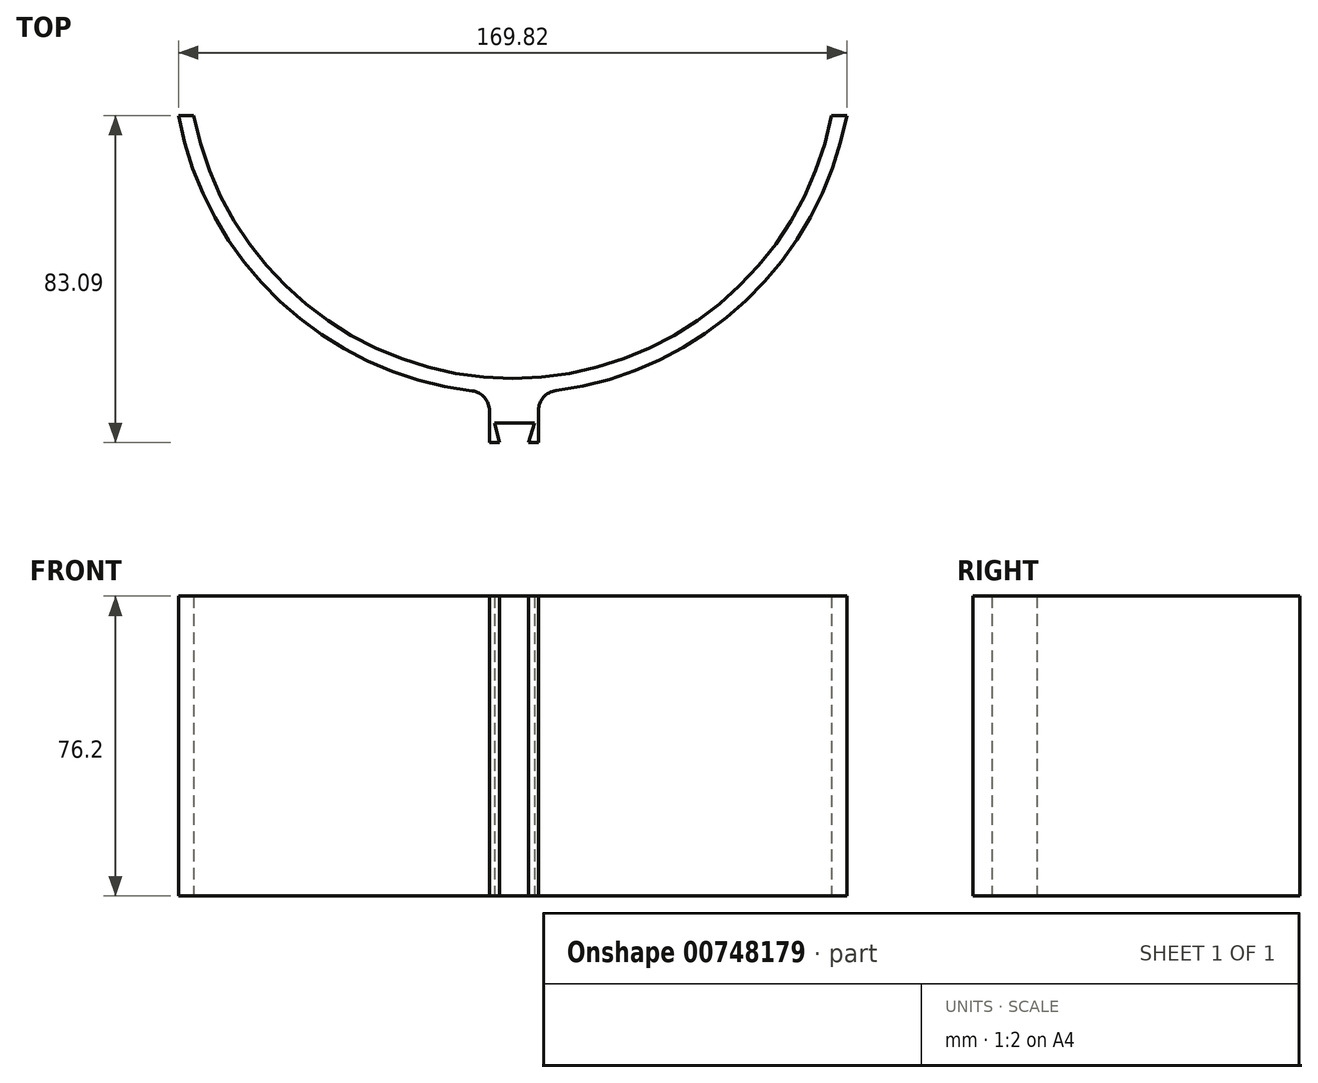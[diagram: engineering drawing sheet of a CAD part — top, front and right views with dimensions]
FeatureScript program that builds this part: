
annotation { "Feature Type Name" : "Feature", "Feature Type Description" : "" }
export const myFeature = defineFeature(function(context is Context, id is Id, definition is map)
    precondition{}
    {
        {
            var Q0;
            Q0=qCreatedBy(makeId("Top.planeOp"),FACE);
            var sketch = newSketch(context, id + "F0", { "sketchPlane" : qUnion([Q0])});
            skArc(sketch, "E0", {"start": v(-81.03, -15.77) * mm, "mid": v(0, -82.55) * mm, "end": v(81.03, -15.77) * mm});
            skArc(sketch, "E1", {"start": v(-84.9, -15.77) * mm, "mid": v(-57.43, -64.5) * mm, "end": v(-5.85, -86.16) * mm});
            skLineSegment(sketch, "E2", {"start": v(6.59, -98.8) * mm, "end": v(6.59, -86.1) * mm});
            skLineSegment(sketch, "E3", {"start": v(-5.85, -86.16) * mm, "end": v(-5.85, -98.86) * mm});
            skArc(sketch, "E4.trimOffspring", {"start": v(6.59, -86.1) * mm, "mid": v(57.7, -64.25) * mm, "end": v(84.9, -15.77) * mm});
            skLineSegment(sketch, "E5", {"start": v(-5.85, -98.86) * mm, "end": v(-3.31, -98.86) * mm});
            skLineSegment(sketch, "E6", {"start": v(-3.31, -98.86) * mm, "end": v(-4.62, -93.95) * mm});
            skLineSegment(sketch, "E7", {"start": v(-4.62, -93.95) * mm, "end": v(5.54, -93.95) * mm});
            skLineSegment(sketch, "E8", {"start": v(5.54, -93.95) * mm, "end": v(4.05, -98.8) * mm});
            skLineSegment(sketch, "E9", {"start": v(4.05, -98.8) * mm, "end": v(6.59, -98.8) * mm});
            skPoint(sketch, "E10.end.orphan", {"position": v(44.56, -136.93) * mm});
            skPoint(sketch, "E11.start.orphan", {"position": v(-44.34, -136.93) * mm});
            skLineSegment(sketch, "E12", {"start": v(-84.9, -15.77) * mm, "end": v(-81.03, -15.77) * mm});
            skLineSegment(sketch, "E13", {"start": v(84.9, -15.77) * mm, "end": v(81.03, -15.77) * mm});
            skLineSegment(sketch, "E14", {"start": v(81.03, -15.77) * mm, "end": v(84.9, -15.77) * mm});
            skPoint(sketch, "E15.start.orphan", {"position": v(-86.36, 0) * mm});
            skSolve(sketch);
        }
        {
            var Q0;
            Q0=makeQuery(id+"F0.imprint","IMPRINT",FACE,{"disambiguationData":[TD([[makeQuery(id+"F0.imprint","IMPRINT",EDGE,{"derivedFrom":sQuery(id+"F0.wireOp",EDGE,"E0")}),-1.0]])]});
            extrude(context, id + "F1", {"entities" : qUnion([Q0]), "endBound" : BoundingType.SYMMETRIC, "depth" : 76.2 * mm, "offsetDistance" : 25.4 * mm});
        }
        {
            var Q0;
            Q0=makeQuery(id+"F1.opExtrude","SWEPT_EDGE",EDGE,{"disambiguationData":[OSD([sQuery(id+"F0.wireOp",EDGE,"E4.trimOffspring"),sQuery(id+"F0.wireOp",EDGE,"E2")])]});
            var Q1;
            Q1=makeQuery(id+"F1.opExtrude","SWEPT_EDGE",EDGE,{"disambiguationData":[OSD([sQuery(id+"F0.wireOp",EDGE,"E1"),sQuery(id+"F0.wireOp",EDGE,"E3")])]});
            fillet(context, id + "F2", {"entities" : qUnion([Q0, Q1]), "radius" : 5.08 * mm, "tangentPropagation" : true, "allowEdgeOverflow" : false});
        }
    });
